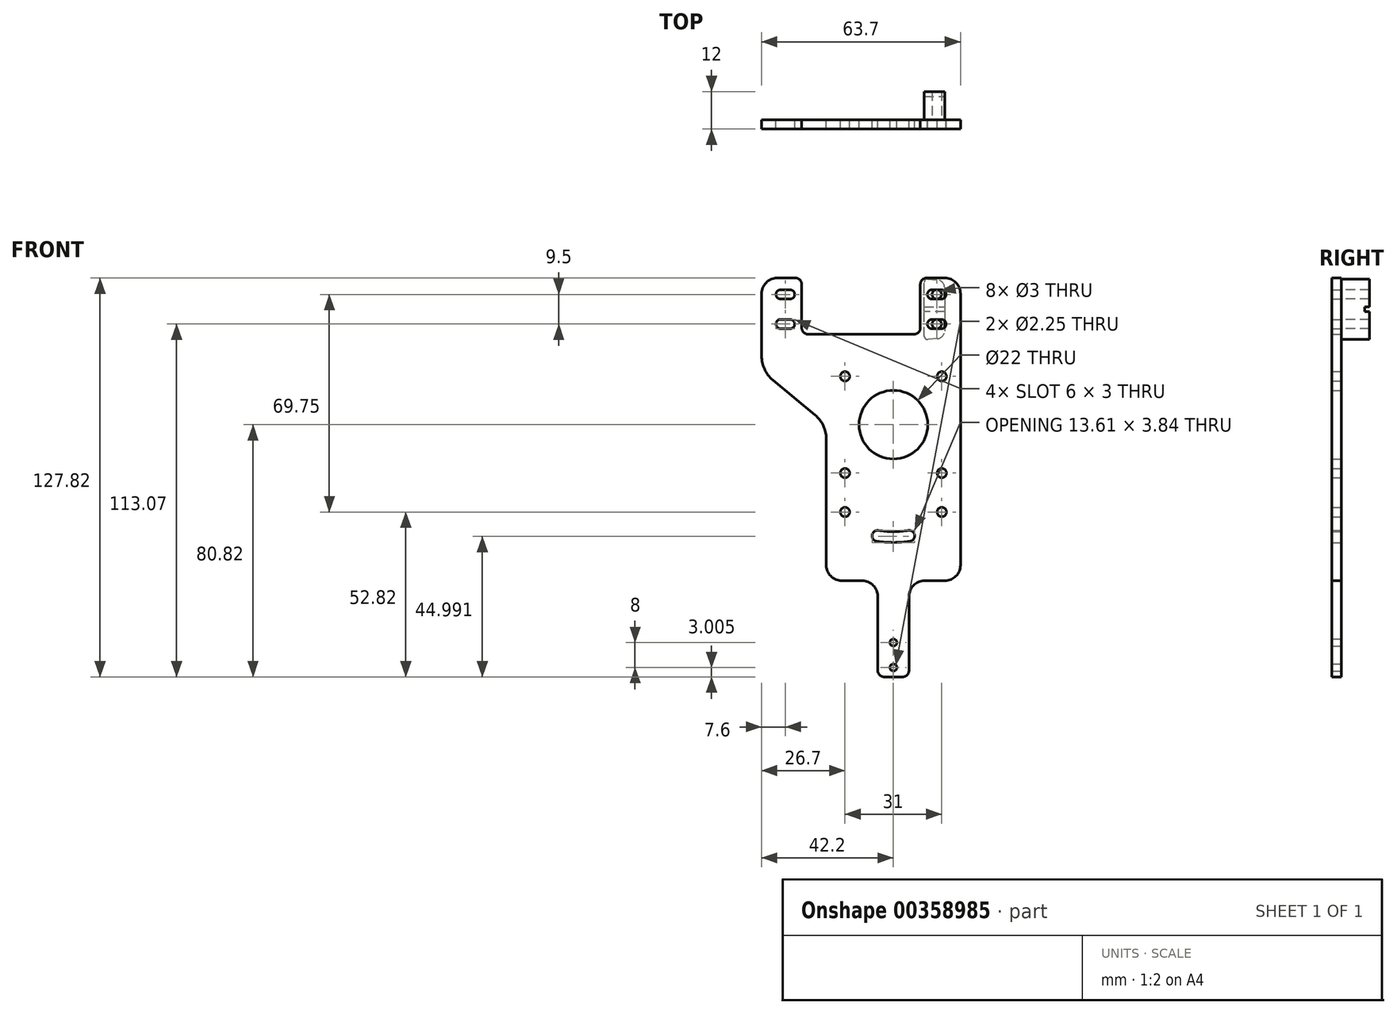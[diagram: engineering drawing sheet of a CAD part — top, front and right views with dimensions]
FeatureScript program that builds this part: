
annotation { "Feature Type Name" : "Feature", "Feature Type Description" : "" }
export const myFeature = defineFeature(function(context is Context, id is Id, definition is map)
    precondition{}
    {
        {
            var Q0;
            Q0=qCreatedBy(makeId("Front.planeOp"),FACE);
            var sketch = newSketch(context, id + "F0", { "sketchPlane" : qUnion([Q0])});
            skLineSegment(sketch, "E0", {"start": v(0, 45.16) * mm, "end": v(0, -78.26) * mm, "construction": true});
            skLineSegment(sketch, "E1", {"start": v(-43, 0) * mm, "end": v(26.64, 0) * mm, "construction": true});
            skCircle(sketch, "E2", {"center": v(0, 0) * mm, "radius": 3.5 * mm, "construction": true});
            skLineSegment(sketch, "E3", {"start": v(-3.05, 24.93) * mm, "end": v(28.89, -79.52) * mm, "construction": true});
            skLineSegment(sketch, "E4", {"start": v(1.45, 7.22) * mm, "end": v(8.27, -15.1) * mm, "construction": true});
            skLineSegment(sketch, "E5", {"start": v(3.28, 7.22) * mm, "end": v(10.1, -15.1) * mm, "construction": true});
            skSolve(sketch);
        }
        {
            var Q0;
            Q0=qCreatedBy(makeId("Front.planeOp"),FACE);
            var sketch = newSketch(context, id + "F1", { "sketchPlane" : qUnion([Q0])});
            skCircle(sketch, "E6", {"center": v(15.5, 15.5) * mm, "radius": 1.5 * mm});
            skLineSegment(sketch, "E7", {"start": v(21.5, -45) * mm, "end": v(21.5, 42) * mm});
            skPoint(sketch, "E8", {"position": v(0, -50) * mm});
            skArc(sketch, "E9", {"start": v(4.83, -33.9) * mm, "mid": v(2.42, -34.16) * mm, "end": v(0, -34.25) * mm});
            skArc(sketch, "E10", {"start": v(5.32, -37.37) * mm, "mid": v(2.67, -37.66) * mm, "end": v(0, -37.75) * mm});
            skArc(sketch, "E11", {"start": v(4.83, -33.9) * mm, "mid": v(6.8, -35.4) * mm, "end": v(5.32, -37.37) * mm});
            skArc(sketch, "E12", {"start": v(8.38, -35) * mm, "mid": v(-0.1, -36) * mm, "end": v(-8.59, -34.96) * mm, "construction": true});
            skCircle(sketch, "E13.MirrorC", {"center": v(15.5, -15.5) * mm, "radius": 1.5 * mm});
            skCircle(sketch, "E14.MirrorC", {"center": v(-15.5, 15.5) * mm, "radius": 1.5 * mm});
            skCircle(sketch, "E15.MirrorC", {"center": v(-15.5, -15.5) * mm, "radius": 1.5 * mm});
            skLineSegment(sketch, "E16.MirrorCS", {"start": v(-21.5, -45) * mm, "end": v(-21.5, -4.56) * mm});
            skArc(sketch, "E17.MirrorCS", {"start": v(-5.32, -37.37) * mm, "mid": v(-2.67, -37.66) * mm, "end": v(0, -37.75) * mm});
            skArc(sketch, "E18.MirrorCS", {"start": v(-4.83, -33.9) * mm, "mid": v(-6.8, -35.4) * mm, "end": v(-5.32, -37.37) * mm});
            skArc(sketch, "E19.MirrorCS", {"start": v(-4.83, -33.9) * mm, "mid": v(-2.42, -34.16) * mm, "end": v(0, -34.25) * mm});
            skLineSegment(sketch, "E20", {"start": v(16.5, 47) * mm, "end": v(10.65, 47) * mm});
            skLineSegment(sketch, "E21", {"start": v(-42.2, 42) * mm, "end": v(-42.2, 22.02) * mm});
            skLineSegment(sketch, "E22", {"start": v(-10.35, 28.4) * mm, "end": v(-10.35, 46.94) * mm, "construction": true});
            skLineSegment(sketch, "E23", {"start": v(22.97, 37) * mm, "end": v(-42.76, 37) * mm, "construction": true});
            skCircle(sketch, "E24", {"center": v(0, 0) * mm, "radius": 11 * mm});
            skLineSegment(sketch, "E25", {"start": v(-16.5, -50) * mm, "end": v(-10, -50) * mm});
            skPoint(sketch, "E26.visualSharp", {"position": v(21.06, 47) * mm});
            skArc(sketch, "E26.filletArc", {"start": v(21.5, 42) * mm, "mid": v(20.04, 45.54) * mm, "end": v(16.5, 47) * mm});
            skPoint(sketch, "E27.visualSharp", {"position": v(-42.2, 47) * mm});
            skArc(sketch, "E27.filletArc", {"start": v(-37.2, 47) * mm, "mid": v(-40.74, 45.54) * mm, "end": v(-42.2, 42) * mm});
            skArc(sketch, "E28", {"start": v(-36.1, 33.75) * mm, "mid": v(-37.6, 32.25) * mm, "end": v(-36.1, 30.75) * mm});
            skLineSegment(sketch, "E29", {"start": v(-38.59, 14.32) * mm, "end": v(-25.11, 3.14) * mm});
            skPoint(sketch, "E30.visualSharp", {"position": v(-21.5, 0.14) * mm});
            skArc(sketch, "E30.filletArc", {"start": v(-21.5, -4.56) * mm, "mid": v(-22.45, -0.3) * mm, "end": v(-25.11, 3.14) * mm});
            skPoint(sketch, "E31.visualSharp", {"position": v(-42.2, 17.32) * mm});
            skArc(sketch, "E31.filletArc", {"start": v(-42.2, 22.02) * mm, "mid": v(-41.25, 17.76) * mm, "end": v(-38.59, 14.32) * mm});
            skArc(sketch, "E32", {"start": v(-33.1, 30.75) * mm, "mid": v(-31.6, 32.25) * mm, "end": v(-33.1, 33.75) * mm});
            skLineSegment(sketch, "E33", {"start": v(-33.1, 33.75) * mm, "end": v(-36.1, 33.75) * mm});
            skLineSegment(sketch, "E34", {"start": v(-33.1, 30.75) * mm, "end": v(-36.1, 30.75) * mm});
            skArc(sketch, "E35.MirrorCS", {"start": v(-36.1, 40.25) * mm, "mid": v(-37.6, 41.75) * mm, "end": v(-36.1, 43.25) * mm});
            skLineSegment(sketch, "E36.MirrorCS", {"start": v(-33.1, 40.25) * mm, "end": v(-36.1, 40.25) * mm});
            skArc(sketch, "E37.MirrorCS", {"start": v(-33.1, 43.25) * mm, "mid": v(-31.6, 41.75) * mm, "end": v(-33.1, 40.25) * mm});
            skLineSegment(sketch, "E38.MirrorCS", {"start": v(-33.1, 43.25) * mm, "end": v(-36.1, 43.25) * mm});
            skArc(sketch, "E39.MirrorCS", {"start": v(12.4, 30.75) * mm, "mid": v(10.9, 32.25) * mm, "end": v(12.4, 33.75) * mm});
            skLineSegment(sketch, "E40.MirrorCS", {"start": v(12.4, 30.75) * mm, "end": v(15.4, 30.75) * mm});
            skLineSegment(sketch, "E41.MirrorCS", {"start": v(12.4, 33.75) * mm, "end": v(15.4, 33.75) * mm});
            skArc(sketch, "E42.MirrorCS", {"start": v(15.4, 33.75) * mm, "mid": v(16.9, 32.25) * mm, "end": v(15.4, 30.75) * mm});
            skLineSegment(sketch, "E43.MirrorCS", {"start": v(12.4, 40.25) * mm, "end": v(15.4, 40.25) * mm});
            skArc(sketch, "E44.MirrorCS", {"start": v(15.4, 40.25) * mm, "mid": v(16.9, 41.75) * mm, "end": v(15.4, 43.25) * mm});
            skArc(sketch, "E45.MirrorCS", {"start": v(12.4, 43.25) * mm, "mid": v(10.9, 41.75) * mm, "end": v(12.4, 40.25) * mm});
            skLineSegment(sketch, "E46.MirrorCS", {"start": v(12.4, 43.25) * mm, "end": v(15.4, 43.25) * mm});
            skCircle(sketch, "E47", {"center": v(5.32, -35.6) * mm, "radius": 1.5 * mm, "construction": true});
            skLineSegment(sketch, "E48", {"start": v(0, 0) * mm, "end": v(6.18, -41.34) * mm, "construction": true});
            skCircle(sketch, "E49", {"center": v(-34.6, 32.25) * mm, "radius": 1.5 * mm, "construction": true});
            skCircle(sketch, "E50.MirrorC", {"center": v(-34.6, 41.75) * mm, "radius": 1.5 * mm, "construction": true});
            skCircle(sketch, "E51.MirrorC", {"center": v(13.9, 32.25) * mm, "radius": 1.5 * mm, "construction": true});
            skCircle(sketch, "E52.MirrorC", {"center": v(13.9, 41.75) * mm, "radius": 1.5 * mm, "construction": true});
            skCircle(sketch, "E53", {"center": v(15.5, -28) * mm, "radius": 1.5 * mm});
            skCircle(sketch, "E54.MirrorC", {"center": v(-15.5, -28) * mm, "radius": 1.5 * mm});
            skLineSegment(sketch, "E55", {"start": v(-27.35, 29) * mm, "end": v(6.65, 29) * mm});
            skLineSegment(sketch, "E56", {"start": v(-29.35, 45) * mm, "end": v(-29.35, 31) * mm});
            skLineSegment(sketch, "E57", {"start": v(8.65, 45) * mm, "end": v(8.65, 31) * mm});
            skLineSegment(sketch, "E58.trimOffspring", {"start": v(-31.35, 47) * mm, "end": v(-37.2, 47) * mm});
            skPoint(sketch, "E59.visualSharp", {"position": v(-29.35, 47) * mm});
            skArc(sketch, "E59.filletArc", {"start": v(-29.35, 45) * mm, "mid": v(-29.94, 46.41) * mm, "end": v(-31.35, 47) * mm});
            skPoint(sketch, "E60.visualSharp", {"position": v(8.65, 47) * mm});
            skArc(sketch, "E60.filletArc", {"start": v(10.65, 47) * mm, "mid": v(9.24, 46.41) * mm, "end": v(8.65, 45) * mm});
            skPoint(sketch, "E61.visualSharp", {"position": v(-29.35, 29) * mm});
            skArc(sketch, "E61.filletArc", {"start": v(-29.35, 31) * mm, "mid": v(-28.76, 29.59) * mm, "end": v(-27.35, 29) * mm});
            skPoint(sketch, "E62.visualSharp", {"position": v(8.65, 29) * mm});
            skArc(sketch, "E62.filletArc", {"start": v(6.65, 29) * mm, "mid": v(8.06, 29.59) * mm, "end": v(8.65, 31) * mm});
            skLineSegment(sketch, "E63", {"start": v(-36.07, -22) * mm, "end": v(-55, -22) * mm, "construction": true});
            skLineSegment(sketch, "E64", {"start": v(-15, -66.45) * mm, "end": v(-53.61, -66.45) * mm, "construction": true});
            skCircle(sketch, "E65", {"center": v(0, -69.82) * mm, "radius": 1.13 * mm});
            skCircle(sketch, "E66", {"center": v(0, -77.82) * mm, "radius": 1.13 * mm});
            skLineSegment(sketch, "E67", {"start": v(-5, -55) * mm, "end": v(-5, -78.82) * mm});
            skLineSegment(sketch, "E68", {"start": v(-3, -80.82) * mm, "end": v(3, -80.82) * mm});
            skLineSegment(sketch, "E69", {"start": v(5, -78.82) * mm, "end": v(5, -55) * mm});
            skLineSegment(sketch, "E70", {"start": v(10, -50) * mm, "end": v(16.5, -50) * mm});
            skPoint(sketch, "E71.visualSharp", {"position": v(-5, -80.82) * mm});
            skArc(sketch, "E71.filletArc", {"start": v(-5, -78.82) * mm, "mid": v(-4.41, -80.23) * mm, "end": v(-3, -80.82) * mm});
            skPoint(sketch, "E72.visualSharp", {"position": v(5, -80.82) * mm});
            skArc(sketch, "E72.filletArc", {"start": v(3, -80.82) * mm, "mid": v(4.41, -80.23) * mm, "end": v(5, -78.82) * mm});
            skPoint(sketch, "E73.visualSharp", {"position": v(-21.5, -50) * mm});
            skArc(sketch, "E73.filletArc", {"start": v(-21.5, -45) * mm, "mid": v(-20.04, -48.54) * mm, "end": v(-16.5, -50) * mm});
            skPoint(sketch, "E74.visualSharp", {"position": v(-5, -50) * mm});
            skArc(sketch, "E74.filletArc", {"start": v(-5, -55) * mm, "mid": v(-6.46, -51.46) * mm, "end": v(-10, -50) * mm});
            skPoint(sketch, "E75.visualSharp", {"position": v(5, -50) * mm});
            skArc(sketch, "E75.filletArc", {"start": v(10, -50) * mm, "mid": v(6.46, -51.46) * mm, "end": v(5, -55) * mm});
            skPoint(sketch, "E76.visualSharp", {"position": v(21.5, -50) * mm});
            skArc(sketch, "E76.filletArc", {"start": v(16.5, -50) * mm, "mid": v(20.04, -48.54) * mm, "end": v(21.5, -45) * mm});
            skSolve(sketch);
        }
        {
            var Q0;
            Q0 = qSketchRegion(id + "F1", true);
            extrude(context, id + "F2", {"entities" : qUnion([Q0]), "depth" : 3 * mm});
        }
        {
            var Q0;
            Q0=qCreatedBy(makeId("Front.planeOp"),FACE);
            var sketch = newSketch(context, id + "F3", { "sketchPlane" : qUnion([Q0])});
            skLineSegment(sketch, "E77", {"start": v(16.4, 46.25) * mm, "end": v(16.4, 27.75) * mm});
            skLineSegment(sketch, "E78", {"start": v(16.4, 27.75) * mm, "end": v(9.9, 27.25) * mm});
            skLineSegment(sketch, "E79", {"start": v(9.9, 27.25) * mm, "end": v(9.9, 46.75) * mm});
            skLineSegment(sketch, "E80", {"start": v(9.9, 46.75) * mm, "end": v(16.4, 46.25) * mm});
            skCircle(sketch, "E81", {"center": v(13.9, 32.25) * mm, "radius": 1.5 * mm});
            skCircle(sketch, "E82.MirrorC", {"center": v(13.9, 41.75) * mm, "radius": 1.5 * mm});
            skLineSegment(sketch, "E83", {"start": v(13.9, 47.55) * mm, "end": v(13.9, 25.9) * mm, "construction": true});
            skSolve(sketch);
        }
        {
            var Q0;
            Q0 = qSketchRegion(id + "F3", true);
            extrude(context, id + "F4", {"entities" : qUnion([Q0]), "oppositeDirection" : true, "depth" : 9 * mm, "offsetDistance" : 25 * mm});
        }
        {
            var Q0;
            Q0=makeQuery(id+"F4.opExtrude","CAP_FACE",FACE,{"disambiguationData":[OSD([sQuery(id+"F3.wireOp",EDGE,"E77"),sQuery(id+"F3.wireOp",EDGE,"E78"),sQuery(id+"F3.wireOp",EDGE,"E79"),sQuery(id+"F3.wireOp",EDGE,"E80"),sQuery(id+"F3.wireOp",EDGE,"E81"),sQuery(id+"F3.wireOp",EDGE,"E82.MirrorC")])],"isStart":false});
            var sketch = newSketch(context, id + "F5", { "sketchPlane" : qUnion([Q0])});
            skLineSegment(sketch, "E84", {"start": v(40.1, -4.41) * mm, "end": v(22.9, -4.41) * mm, "construction": true});
            skLineSegment(sketch, "E85", {"start": v(-9.9, 36.25) * mm, "end": v(-9.9, 37.75) * mm});
            skLineSegment(sketch, "E86", {"start": v(-9.9, 37.75) * mm, "end": v(-16.4, 37.75) * mm});
            skLineSegment(sketch, "E87", {"start": v(-16.4, 37.75) * mm, "end": v(-16.4, 36.25) * mm});
            skLineSegment(sketch, "E88", {"start": v(-16.4, 36.25) * mm, "end": v(-9.9, 36.25) * mm});
            skSolve(sketch);
        }
        {
            var Q0;
            Q0 = qSketchRegion(id + "F5", true);
            extrude(context, id + "F6", {"entities" : qUnion([Q0]), "operationType" : NewBodyOperationType.REMOVE, "oppositeDirection" : true, "depth" : 1.5 * mm});
        }
        {
            var Q0;
            Q0=makeQuery(id+"F4.opExtrude","SWEPT_EDGE",EDGE,{"disambiguationData":[OSD([sQuery(id+"F3.wireOp",EDGE,"E79"),sQuery(id+"F3.wireOp",EDGE,"E80")])]});
            var Q1;
            Q1=makeQuery(id+"F4.opExtrude","SWEPT_EDGE",EDGE,{"disambiguationData":[OSD([sQuery(id+"F3.wireOp",EDGE,"E78"),sQuery(id+"F3.wireOp",EDGE,"E79")])]});
            fillet(context, id + "F7", {"entities" : qUnion([Q0, Q1]), "radius" : 1 * mm, "tangentPropagation" : true, "allowEdgeOverflow" : false});
        }
        {
            var Q0;
            Q0=makeQuery(id+"F4.opExtrude","SWEPT_EDGE",EDGE,{"disambiguationData":[OSD([sQuery(id+"F3.wireOp",EDGE,"E77"),sQuery(id+"F3.wireOp",EDGE,"E78")])]});
            var Q1;
            Q1=makeQuery(id+"F4.opExtrude","SWEPT_EDGE",EDGE,{"disambiguationData":[OSD([sQuery(id+"F3.wireOp",EDGE,"E77"),sQuery(id+"F3.wireOp",EDGE,"E80")])]});
            fillet(context, id + "F8", {"entities" : qUnion([Q0, Q1]), "radius" : 2.5 * mm, "tangentPropagation" : true, "allowEdgeOverflow" : false});
        }
    });
